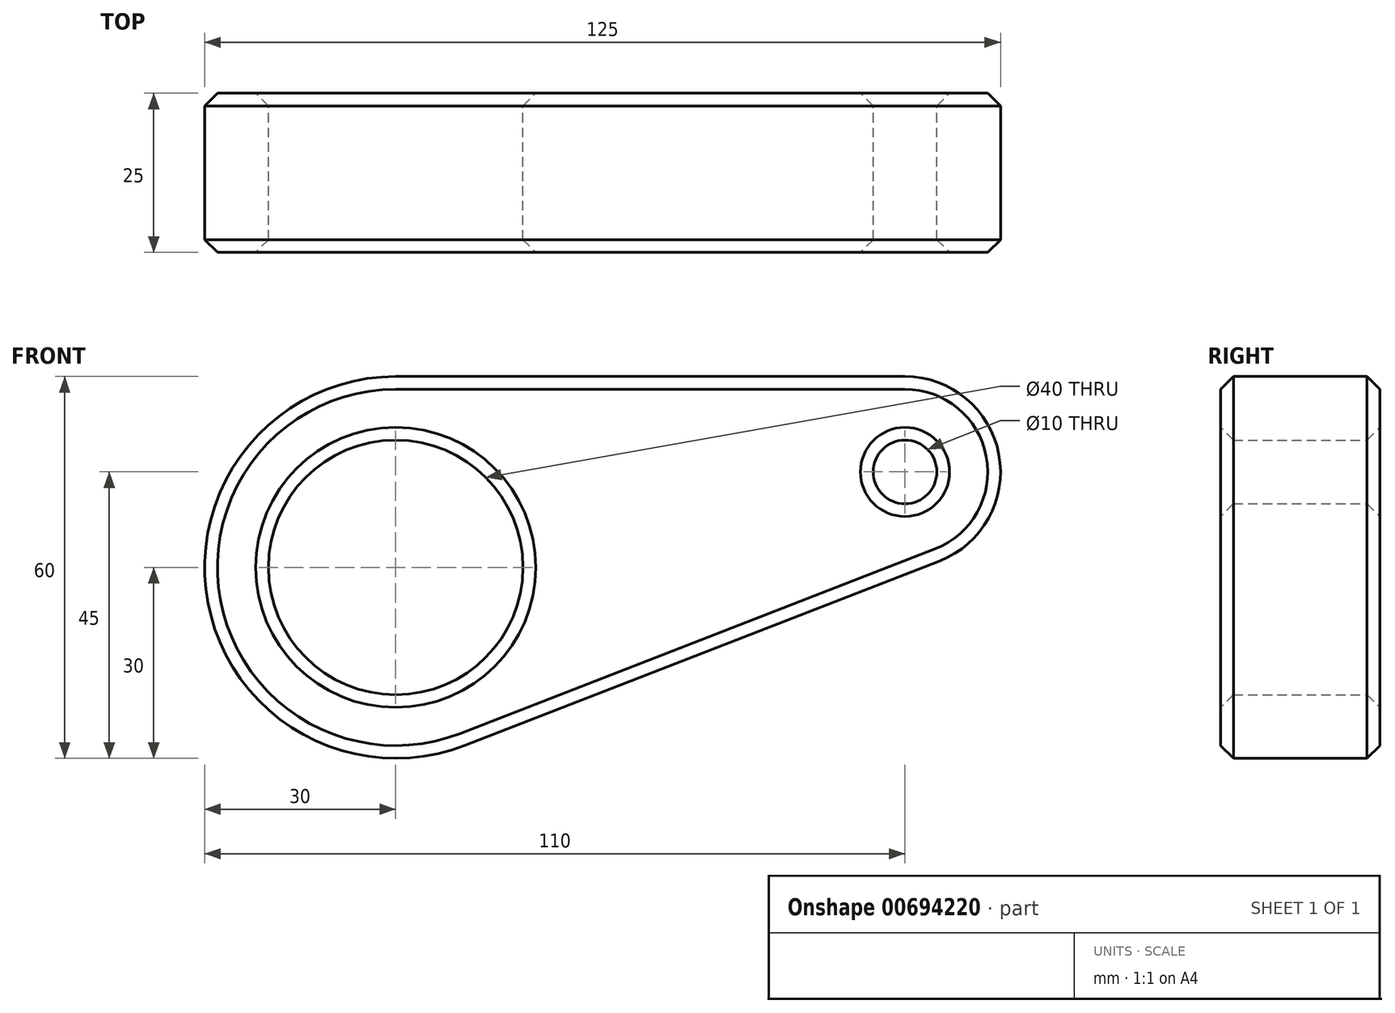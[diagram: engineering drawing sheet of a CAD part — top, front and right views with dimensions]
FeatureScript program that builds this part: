
annotation { "Feature Type Name" : "Feature", "Feature Type Description" : "" }
export const myFeature = defineFeature(function(context is Context, id is Id, definition is map)
    precondition{}
    {
        {
            var Q0;
            Q0=qCreatedBy(makeId("Front.planeOp"),FACE);
            var sketch = newSketch(context, id + "F0", { "sketchPlane" : qUnion([Q0])});
            skCircle(sketch, "E0", {"center": v(0, 0) * mm, "radius": 30 * mm});
            skCircle(sketch, "E1", {"center": v(80, 15) * mm, "radius": 15 * mm});
            skCircle(sketch, "E2.0", {"center": v(0, 0) * mm, "radius": 20 * mm});
            skCircle(sketch, "E3.0", {"center": v(80, 15) * mm, "radius": 5 * mm});
            skLineSegment(sketch, "E4", {"start": v(10.87, -27.96) * mm, "end": v(85.43, 1.02) * mm});
            skLineSegment(sketch, "E5", {"start": v(0, 30) * mm, "end": v(80, 30) * mm});
            skSolve(sketch);
        }
        {
            var Q0;
            Q0=makeQuery(id+"F0.imprint","IMPRINT",FACE,{"disambiguationData":[TD([[makeQuery(id+"F0.imprint","IMPRINT",EDGE,{"derivedFrom":sQuery(id+"F0.wireOp",EDGE,"E2.0")}),-1.0]])]});
            var Q1;
            {var subQ0=sQuery(id+"F0.wireOp",EDGE,"E4");Q1=makeQuery(id+"F0.imprint","IMPRINT",FACE,{"disambiguationData":[TD([[makeQuery(id+"F0.imprint","IMPRINT",EDGE,{"derivedFrom":subQ0}),1.0]])]});}
            var Q2;
            Q2=makeQuery(id+"F0.imprint","IMPRINT",FACE,{"disambiguationData":[TD([[makeQuery(id+"F0.imprint","IMPRINT",EDGE,{"derivedFrom":sQuery(id+"F0.wireOp",EDGE,"E3.0")}),-1.0]])]});
            extrude(context, id + "F1", {"entities" : qUnion([Q0, Q1, Q2]), "depth" : 25 * mm, "offsetDistance" : 25 * mm});
        }
        {
            var Q0;
            Q0=makeQuery(id+"F1.opExtrude","CAP_EDGE",EDGE,{"disambiguationData":[OSD([sQuery(id+"F0.wireOp",EDGE,"E2.0")])],"isStart":false});
            var Q1;
            Q1=makeQuery(id+"F1.opExtrude","CAP_EDGE",EDGE,{"disambiguationData":[OSD([sQuery(id+"F0.wireOp",EDGE,"E3.0")])],"isStart":false});
            var Q2;
            Q2=makeQuery(id+"F1.opExtrude","CAP_EDGE",EDGE,{"disambiguationData":[OSD([sQuery(id+"F0.wireOp",EDGE,"E2.0")])],"isStart":true});
            var Q3;
            Q3=makeQuery(id+"F1.opExtrude","CAP_EDGE",EDGE,{"disambiguationData":[OSD([sQuery(id+"F0.wireOp",EDGE,"E3.0")])],"isStart":true});
            var Q4;
            Q4=makeQuery(id+"F1.opExtrude","CAP_EDGE",EDGE,{"disambiguationData":[OSD([sQuery(id+"F0.wireOp",EDGE,"E5")])],"isStart":true});
            var Q5;
            Q5=makeQuery(id+"F1.opExtrude","CAP_EDGE",EDGE,{"disambiguationData":[OSD([sQuery(id+"F0.wireOp",EDGE,"E5")])],"isStart":false});
            chamfer(context, id + "F2", {"entities" : qUnion([Q0, Q1, Q2, Q3, Q4, Q5]), "width" : 2 * mm, "tangentPropagation" : true});
        }
    });
